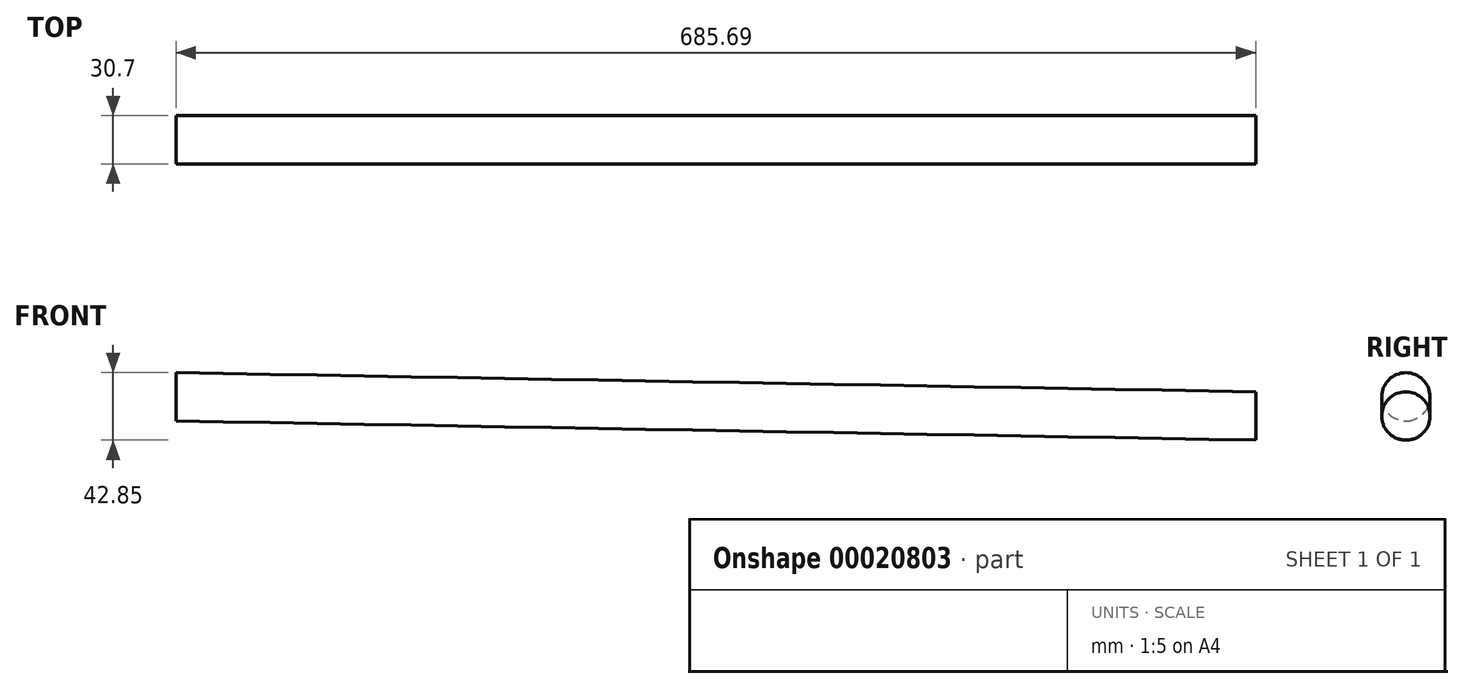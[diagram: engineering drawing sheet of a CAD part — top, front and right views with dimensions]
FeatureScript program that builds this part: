
annotation { "Feature Type Name" : "Feature", "Feature Type Description" : "" }
export const myFeature = defineFeature(function(context is Context, id is Id, definition is map)
    precondition{}
    {
        {
            var Q0;
            Q0=qCreatedBy(makeId("Front.planeOp"),FACE);
            var sketch = newSketch(context, id + "F0", { "sketchPlane" : qUnion([Q0])});
            skLineSegment(sketch, "E0", {"start": v(-343.97, 10.1) * mm, "end": v(341.72, -2.05) * mm});
            skSolve(sketch);
        }
        {
            var Q0;
            Q0=qCreatedBy(makeId("Right.planeOp"),FACE);
            cPlane(context, id + "F1", {"entities" : qUnion([Q0]), "cplaneType" : CPlaneType.OFFSET, "offset" : 341.88 * mm, "width" : 152.4 * mm, "height" : 152.4 * mm});
        }
        {
            var Q0;
            Q0=qCreatedBy(id+"F1.planeOp",FACE);
            var sketch = newSketch(context, id + "F2", { "sketchPlane" : qUnion([Q0])});
            skCircle(sketch, "E1", {"center": v(0, -2.05) * mm, "radius": 15.35 * mm});
            skSolve(sketch);
        }
        {
            var Q0;
            Q0=makeQuery(id+"F2.imprint","IMPRINT",FACE,{"disambiguationData":[TD([[makeQuery(id+"F2.imprint","IMPRINT",EDGE,{"derivedFrom":sQuery(id+"F2.wireOp",EDGE,"E1")}),1.0]])]});
            var Q1;
            Q1=sQuery(id+"F0.wireOp",EDGE,"E0");
            sweep(context, id + "F3", {"profiles" : qUnion([Q0]), "path" : qUnion([Q1])});
        }
    });
